# Revit family: Shower-Shower_Column_Kit-KOHLER-HydroRail-K-76474_1
name_source: partatom
category: Plumbing Fixtures
units: mm (PartAtom-declared; Revit-internal decimal feet)

## family parameters
Cut with Voids When Loaded = No
Host = Face
OmniClass Number = 23.31.17.00
OmniClass Title = Showers
Part Type = Normal
Room Calculation Point = No
Round Connector Dimension = Use Diameter
Shared = No

## types (6) — shared parameters
ADA Compliant = No
Assembly Code = D2010700
CW Connection = No
Cold Water Inlet = Cold Water Inlet
Date Modified = 11/13/2022
Default Elevation = 42"
Drain Included = No
HW Connection = Yes
Height = 27 1/2"
Hot Water Inlet = Hot Water Inlet
Length = 17 15/16"
Manufacturer = Kohler Co.
Master Format 2014 = 22 42 23
Master Format 2014 Name = Residential Showers
Material = Premium Metal Construction
Panel Thickness = 0"
Pressure = 80.00 psi
Product Documentation Link = https://www.us.kohler.com
Product Name = HydroRail R
Product Page URL = http://www.us.kohler.com
Tempered Water Inlet = Tempered Water Inlet
URL = http://www.us.kohler.com
Vent Connection = No
Waste Connection = No
Waste Water Outlet = Waste Water Outlet
WaterSense Certified = No
Width = 8"

## per-type parameters (varying)
| type | 2.0 GPM | 2.5 GPM | Description | Finish | Flow Rate | Model | Secondary Finish | Type |
| 2.0 GPM, BL-Matte Black | Yes | No | Awaken Shift Ellipse Arch Shower Column Kit With Rainhead and 2.0 gpm Handshower | Kohler-Metal-BL-Matte_Black | 2 GPM | K-76474-BL | Kohler-Plastic-58-Thunder_Grey | 1 |
| 2.0 GPM, BN-Vibrant Brushed Nickel | Yes | No | Awaken Shift Ellipse Arch Shower Column Kit With Rainhead and 2.0 gpm Handshower | Kohler-Metal-BN-Vibrant_Brushed_Nickel | 2 GPM | K-76474-BN | Kohler-Plastic-0-White | 2 |
| 2.0 GPM, CP-Polished Chrome | Yes | No | Awaken Shift Ellipse Arch Shower Column Kit With Rainhead and 2.0 gpm Handshower | Kohler-Metal-CP-Polished_Chrome | 2 GPM | K-76474-CP | Kohler-Plastic-0-White | 3 |
| 2.5 GPM, BL-Matte Black | No | Yes | Contemporary Round Hydrorail Kit | Kohler-Metal-BL-Matte_Black | 3 GPM | K-76474-Y-BL | Kohler-Plastic-58-Thunder_Grey | 4 |
| 2.5 GPM, BN-Vibrant Brushed Nickel | No | Yes | Contemporary Round Hydrorail Kit | Kohler-Metal-BN-Vibrant_Brushed_Nickel | 3 GPM | K-76474-Y-BN | Kohler-Plastic-0-White | 5 |
| 2.5 GPM, CP-Polished Chrome | No | Yes | Contemporary Round Hydrorail Kit | Kohler-Metal-CP-Polished_Chrome | 3 GPM | K-76474-Y-CP | Kohler-Plastic-0-White | 6 |

## geometry (parser evidence)
native form markers: Sweep x6
no freeform markers — native parametric forms only
